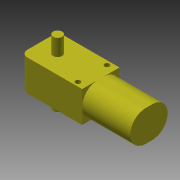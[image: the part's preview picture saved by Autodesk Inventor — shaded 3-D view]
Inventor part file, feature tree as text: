
AUTODESK INVENTOR PART (.ipt)
format: ipt  version: 2015 (Build 190159000, 159)  size: 161,792 bytes
history: native  units: mm
features: extrude x7, sketch x7, fillet x1, hole x1
ambient origin geometry x8: Origin, YZ Plane, XZ Plane, XY Plane, X Axis, Y Axis, Z Axis, Center Point
bodies: Volumenkörper1 (feature_tree)
feature tree (16):
  extrude  "Extrusion1"  Depth=22.5mm
  extrude  "Extrusion2"  Depth=29.0mm TaperAngle=0.0deg
  extrude  "Extrusion3"  Depth=11.25mm
  extrude  "Extrusion4"  Depth=10.0mm
  extrude  "Extrusion5"  Depth=11.25mm
  extrude  "Extrusion6"  Depth=4.0mm
  fillet  "Rundung1"  Radius=11.25mm
  extrude  "Extrusion7"  Depth=8.0mm
  hole  "Bohrung1"  [1 undecoded]
  sketch  "Skizze1"  dims[d0=37.0mm d1=22.5mm]
  sketch  "Skizze2"  dims[d2=18.7mm d3=0.0mm d4=29.0mm d5=0.0mm]
  sketch  "Skizze3"  dims[d6=11.0mm d7=11.25mm]
  sketch  "Skizze4"  dims[d8=10.0mm d9=0.0mm d10=5.5mm]
  sketch  "Skizze5"  dims[d11=11.0mm d12=11.25mm]
  sketch  "Skizze6"  dims[d13=10.0mm d14=0.0mm d15=4.0mm d16=11.25mm]
  sketch  "Skizze7"  dims[d17=22.5mm d18=11.25mm d19=2.0mm d20=0.0mm d21=5.5mm d22=3.0mm d23=5.0mm d25=18.7mm d26=7.85mm d27=7.85mm d28=5.0mm d29=0.0mm d30=4.0mm d31=2.5mm d32=2.5mm d33=32.0mm d34=32.0mm d35=3.0mm d36=3.0mm d37=10.0mm d38=0.0mm d39=2.5mm d40=2.5mm d41=3.0mm d42=6.0mm d43=4.0mm d44=2.0mm d45=90.0deg d46=8.0mm d47=20.594885mm]
note: 1 required parameter value undecoded (feature->parameter linkage not recoverable at this tier; creation-order binding heuristic only, values carry confidence <= 0.55)
